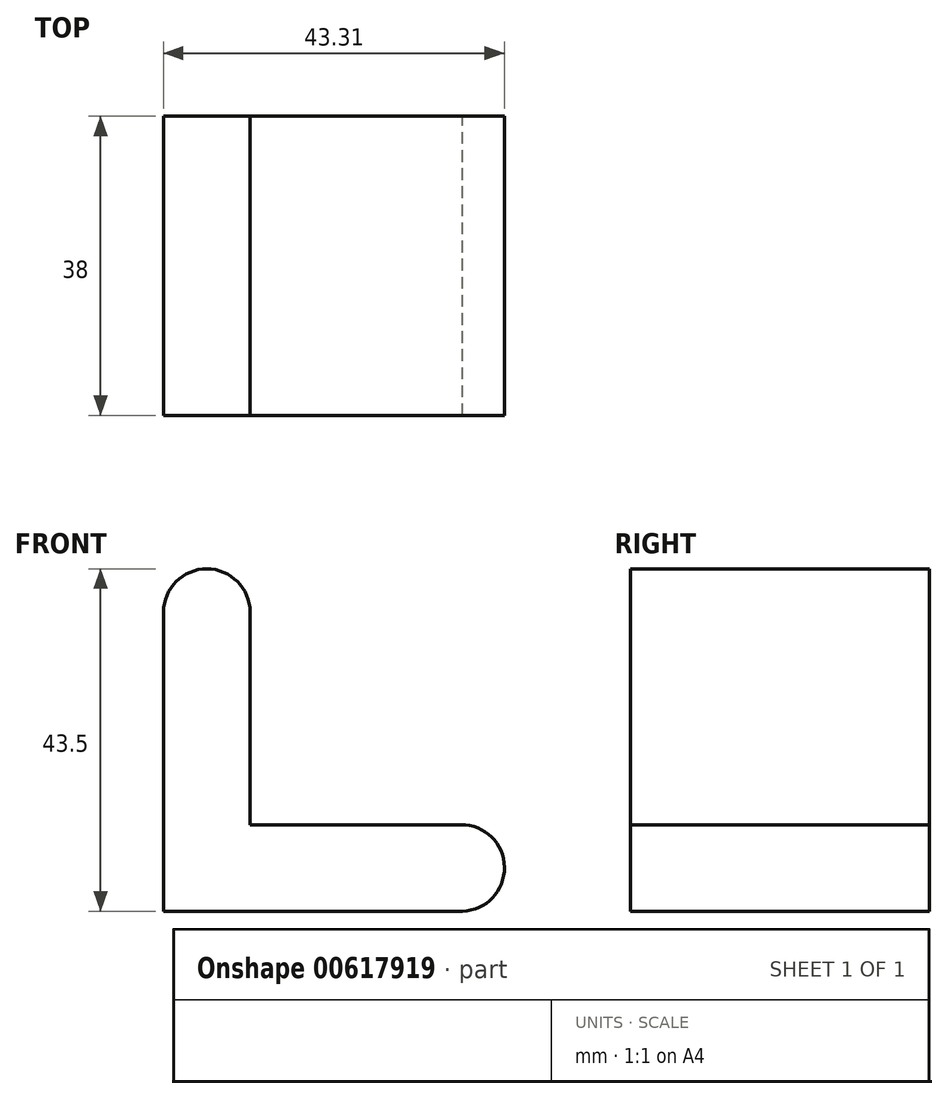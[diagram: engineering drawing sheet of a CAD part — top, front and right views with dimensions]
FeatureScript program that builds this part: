
annotation { "Feature Type Name" : "Feature", "Feature Type Description" : "" }
export const myFeature = defineFeature(function(context is Context, id is Id, definition is map)
    precondition{}
    {
        {
            var Q0;
            Q0=qCreatedBy(makeId("Front.planeOp"),FACE);
            var sketch = newSketch(context, id + "F0", { "sketchPlane" : qUnion([Q0])});
            skLineSegment(sketch, "E0", {"start": v(0, 0) * mm, "end": v(38, 0) * mm});
            skLineSegment(sketch, "E1", {"start": v(0, 0) * mm, "end": v(0, 38) * mm});
            skLineSegment(sketch, "E2", {"start": v(11, 38) * mm, "end": v(11, 11) * mm});
            skLineSegment(sketch, "E3", {"start": v(11, 11) * mm, "end": v(37.81, 11) * mm});
            skArc(sketch, "E4", {"start": v(0, 38) * mm, "mid": v(5.5, 43.5) * mm, "end": v(11, 38) * mm});
            skArc(sketch, "E5", {"start": v(37.81, 11) * mm, "mid": v(43.31, 5.6) * mm, "end": v(38, 0) * mm});
            skSolve(sketch);
        }
        {
            var Q0;
            Q0 = qSketchRegion(id + "F0", true);
            extrude(context, id + "F1", {"entities" : qUnion([Q0]), "depth" : 38 * mm, "offsetDistance" : 25.4 * mm});
        }
    });
